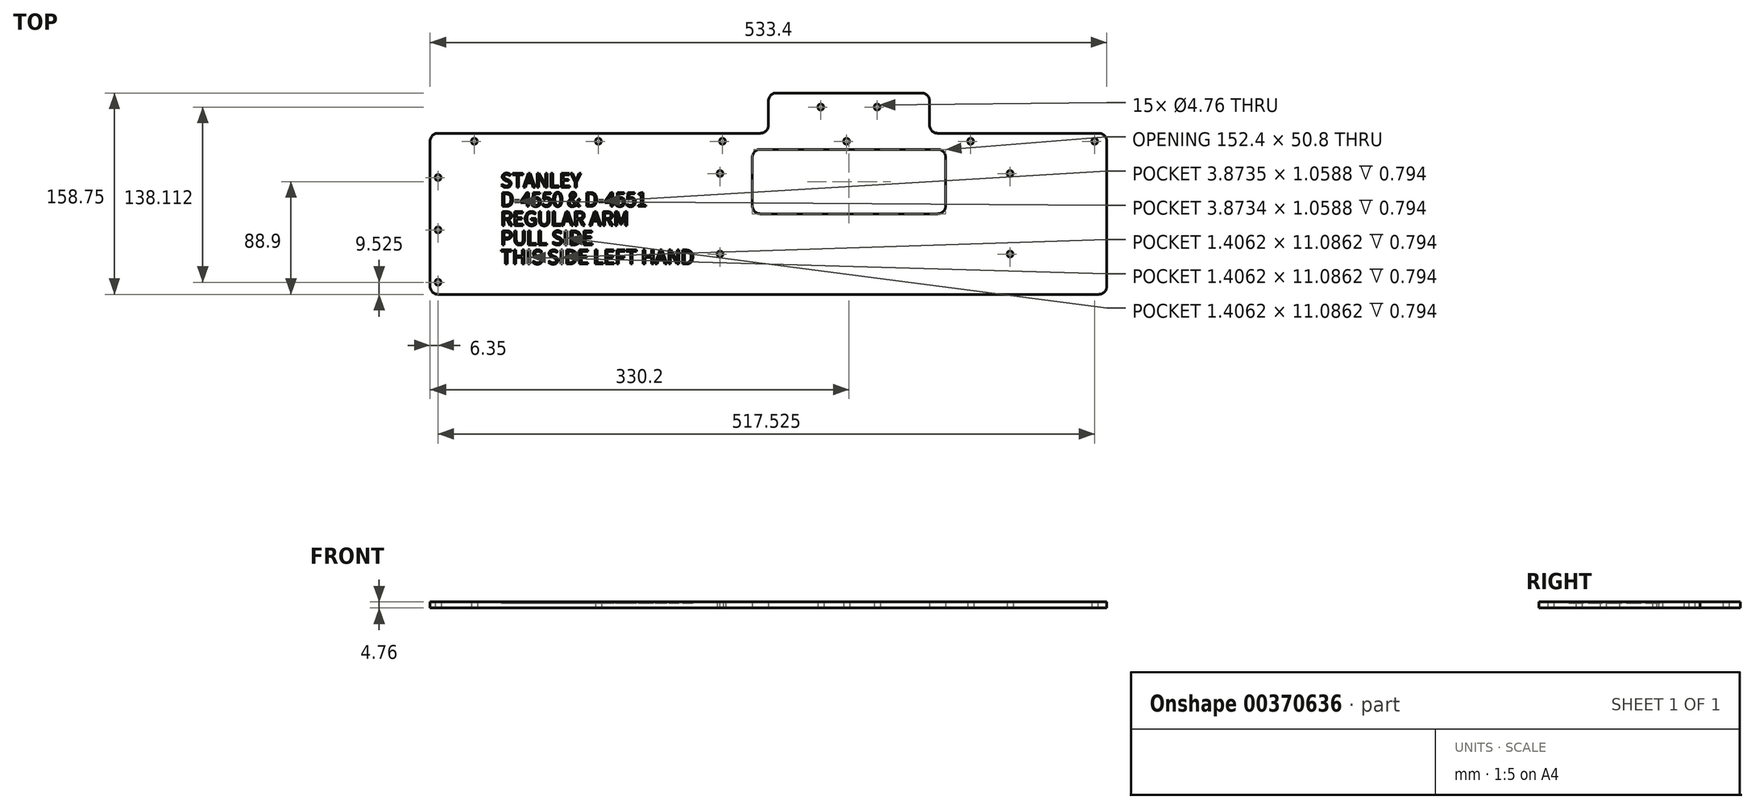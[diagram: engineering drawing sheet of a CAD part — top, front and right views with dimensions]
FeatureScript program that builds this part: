
annotation { "Feature Type Name" : "Feature", "Feature Type Description" : "" }
export const myFeature = defineFeature(function(context is Context, id is Id, definition is map)
    precondition{}
    {
        {
            var Q0;
            Q0=qCreatedBy(makeId("Top.planeOp"),FACE);
            var sketch = newSketch(context, id + "F0", { "sketchPlane" : qUnion([Q0])});
            skLineSegment(sketch, "E0.bottom", {"start": v(6.35, 0) * mm, "end": v(527.05, 0) * mm});
            skLineSegment(sketch, "E0.top", {"start": v(6.35, 127) * mm, "end": v(260.35, 127) * mm});
            skLineSegment(sketch, "E0.left", {"start": v(0, 6.35) * mm, "end": v(0, 120.65) * mm});
            skLineSegment(sketch, "E0.right", {"start": v(533.4, 6.35) * mm, "end": v(533.4, 120.65) * mm});
            skCircle(sketch, "E1", {"center": v(228.6, 95.25) * mm, "radius": 2.38 * mm});
            skCircle(sketch, "E2", {"center": v(228.6, 31.75) * mm, "radius": 2.38 * mm});
            skCircle(sketch, "E3", {"center": v(457.2, 95.25) * mm, "radius": 2.38 * mm});
            skCircle(sketch, "E4", {"center": v(457.2, 31.75) * mm, "radius": 2.38 * mm});
            skLineSegment(sketch, "E5", {"start": v(0, 114.3) * mm, "end": v(533.4, 114.3) * mm, "construction": true});
            skLineSegment(sketch, "E6.0", {"start": v(0, 101.6) * mm, "end": v(648.77, 101.6) * mm, "construction": true});
            skLineSegment(sketch, "E7.0", {"start": v(12.7, 0) * mm, "end": v(12.7, 127) * mm, "construction": true});
            skLineSegment(sketch, "E8.0", {"start": v(25.4, 0) * mm, "end": v(25.4, 127) * mm, "construction": true});
            skLineSegment(sketch, "E9.0", {"start": v(330.2, 127) * mm, "end": v(330.2, 267.26) * mm, "construction": true});
            skLineSegment(sketch, "E10.0", {"start": v(393.7, 133.35) * mm, "end": v(393.7, 152.4) * mm});
            skLineSegment(sketch, "E11.0", {"start": v(266.7, 133.35) * mm, "end": v(266.7, 152.4) * mm});
            skLineSegment(sketch, "E12.0", {"start": v(273.05, 158.75) * mm, "end": v(387.35, 158.75) * mm});
            skArc(sketch, "E13.filletArc", {"start": v(273.05, 158.75) * mm, "mid": v(268.56, 156.9) * mm, "end": v(266.7, 152.4) * mm});
            skLineSegment(sketch, "E14.trimOffspring", {"start": v(400.05, 127) * mm, "end": v(527.05, 127) * mm});
            skPoint(sketch, "E15.visualSharp", {"position": v(266.7, 127) * mm});
            skArc(sketch, "E15.filletArc", {"start": v(260.35, 127) * mm, "mid": v(264.84, 128.86) * mm, "end": v(266.7, 133.35) * mm});
            skArc(sketch, "E16.filletArc", {"start": v(393.7, 152.4) * mm, "mid": v(391.84, 156.9) * mm, "end": v(387.35, 158.75) * mm});
            skPoint(sketch, "E17.visualSharp", {"position": v(393.7, 127) * mm});
            skArc(sketch, "E17.filletArc", {"start": v(393.7, 133.35) * mm, "mid": v(395.56, 128.86) * mm, "end": v(400.05, 127) * mm});
            skCircle(sketch, "E18", {"center": v(307.98, 147.64) * mm, "radius": 2.38 * mm});
            skCircle(sketch, "E19", {"center": v(352.42, 147.64) * mm, "radius": 2.38 * mm});
            skLineSegment(sketch, "E20", {"start": v(307.98, 147.64) * mm, "end": v(352.42, 147.64) * mm, "construction": true});
            skPoint(sketch, "E21", {"position": v(330.2, 147.64) * mm});
            skPoint(sketch, "E22.visualSharp", {"position": v(0, 127) * mm});
            skArc(sketch, "E22.filletArc", {"start": v(6.35, 127) * mm, "mid": v(1.86, 125.14) * mm, "end": v(0, 120.65) * mm});
            skPoint(sketch, "E23.visualSharp", {"position": v(0, 0) * mm});
            skArc(sketch, "E23.filletArc", {"start": v(0, 6.35) * mm, "mid": v(1.86, 1.86) * mm, "end": v(6.35, 0) * mm});
            skPoint(sketch, "E24.visualSharp", {"position": v(533.4, 0) * mm});
            skArc(sketch, "E24.filletArc", {"start": v(527.05, 0) * mm, "mid": v(531.54, 1.86) * mm, "end": v(533.4, 6.35) * mm});
            skPoint(sketch, "E25.visualSharp", {"position": v(533.4, 127) * mm});
            skArc(sketch, "E25.filletArc", {"start": v(533.4, 120.65) * mm, "mid": v(531.54, 125.14) * mm, "end": v(527.05, 127) * mm});
            skCircle(sketch, "E26", {"center": v(6.35, 9.53) * mm, "radius": 2.38 * mm});
            skCircle(sketch, "E27", {"center": v(6.35, 50.8) * mm, "radius": 2.38 * mm});
            skCircle(sketch, "E28", {"center": v(6.35, 92.08) * mm, "radius": 2.38 * mm});
            skCircle(sketch, "E29", {"center": v(34.92, 120.65) * mm, "radius": 2.38 * mm});
            skCircle(sketch, "E30", {"center": v(132.72, 120.65) * mm, "radius": 2.38 * mm});
            skCircle(sketch, "E31", {"center": v(230.5, 120.65) * mm, "radius": 2.38 * mm});
            skCircle(sketch, "E32", {"center": v(328.3, 120.65) * mm, "radius": 2.38 * mm});
            skCircle(sketch, "E33", {"center": v(426.09, 120.65) * mm, "radius": 2.38 * mm});
            skCircle(sketch, "E34", {"center": v(523.88, 120.65) * mm, "radius": 2.38 * mm});
            skLineSegment(sketch, "E35", {"start": v(34.92, 120.65) * mm, "end": v(132.72, 120.65) * mm, "construction": true});
            skLineSegment(sketch, "E36", {"start": v(132.72, 120.65) * mm, "end": v(230.5, 120.65) * mm, "construction": true});
            skLineSegment(sketch, "E37", {"start": v(230.5, 120.65) * mm, "end": v(328.3, 120.65) * mm, "construction": true});
            skLineSegment(sketch, "E38", {"start": v(328.3, 120.65) * mm, "end": v(426.09, 120.65) * mm, "construction": true});
            skLineSegment(sketch, "E39", {"start": v(426.09, 120.65) * mm, "end": v(523.88, 120.65) * mm, "construction": true});
            skLineSegment(sketch, "E40", {"start": v(6.35, 92.08) * mm, "end": v(6.35, 50.8) * mm, "construction": true});
            skLineSegment(sketch, "E41", {"start": v(6.35, 50.8) * mm, "end": v(6.35, 9.53) * mm, "construction": true});
            skLineSegment(sketch, "E42.bottom", {"start": v(260.35, 114.3) * mm, "end": v(400.05, 114.3) * mm});
            skLineSegment(sketch, "E42.top", {"start": v(260.35, 63.5) * mm, "end": v(400.05, 63.5) * mm});
            skLineSegment(sketch, "E42.left", {"start": v(254, 107.95) * mm, "end": v(254, 69.85) * mm});
            skLineSegment(sketch, "E42.right", {"start": v(406.4, 107.95) * mm, "end": v(406.4, 69.85) * mm});
            skPoint(sketch, "E43.visualSharp", {"position": v(254, 114.3) * mm});
            skArc(sketch, "E43.filletArc", {"start": v(260.35, 114.3) * mm, "mid": v(255.86, 112.44) * mm, "end": v(254, 107.95) * mm});
            skPoint(sketch, "E44.visualSharp", {"position": v(254, 63.5) * mm});
            skArc(sketch, "E44.filletArc", {"start": v(254, 69.85) * mm, "mid": v(255.86, 65.36) * mm, "end": v(260.35, 63.5) * mm});
            skPoint(sketch, "E45.visualSharp", {"position": v(406.4, 63.5) * mm});
            skArc(sketch, "E45.filletArc", {"start": v(400.05, 63.5) * mm, "mid": v(404.54, 65.36) * mm, "end": v(406.4, 69.85) * mm});
            skPoint(sketch, "E46.visualSharp", {"position": v(406.4, 114.3) * mm});
            skArc(sketch, "E46.filletArc", {"start": v(406.4, 107.95) * mm, "mid": v(404.54, 112.44) * mm, "end": v(400.05, 114.3) * mm});
            skSolve(sketch);
        }
        {
            var Q0;
            Q0=qSketchRegion(id+"F0",true);
            extrude(context, id + "F1", {"entities" : qUnion([Q0]), "depth" : 4.76 * mm});
        }
        {
            var Q0;
            Q0=makeQuery(id+"F1.opExtrude","CAP_FACE",FACE,{"disambiguationData":[OSD([sQuery(id+"F0.wireOp",EDGE,"E0.bottom"),sQuery(id+"F0.wireOp",EDGE,"E0.top"),sQuery(id+"F0.wireOp",EDGE,"E0.left"),sQuery(id+"F0.wireOp",EDGE,"E0.right"),sQuery(id+"F0.wireOp",EDGE,"E1"),sQuery(id+"F0.wireOp",EDGE,"E2"),sQuery(id+"F0.wireOp",EDGE,"E3"),sQuery(id+"F0.wireOp",EDGE,"E4"),sQuery(id+"F0.wireOp",EDGE,"E10.0"),sQuery(id+"F0.wireOp",EDGE,"E11.0"),sQuery(id+"F0.wireOp",EDGE,"E12.0"),sQuery(id+"F0.wireOp",EDGE,"E13.filletArc"),sQuery(id+"F0.wireOp",EDGE,"E14.trimOffspring"),sQuery(id+"F0.wireOp",EDGE,"E15.filletArc"),sQuery(id+"F0.wireOp",EDGE,"E16.filletArc"),sQuery(id+"F0.wireOp",EDGE,"E17.filletArc"),sQuery(id+"F0.wireOp",EDGE,"E18"),sQuery(id+"F0.wireOp",EDGE,"8vzgHWK5-CGjt-0HD0-FSng-8EKi4hqDK3IT"),sQuery(id+"F0.wireOp",EDGE,"UmFmnjl2-O3XH-EXjj-iWft-K4RkXt2c9gUR"),sQuery(id+"F0.wireOp",EDGE,"E19"),sQuery(id+"F0.wireOp",EDGE,"E22.filletArc"),sQuery(id+"F0.wireOp",EDGE,"E23.filletArc"),sQuery(id+"F0.wireOp",EDGE,"E24.filletArc"),sQuery(id+"F0.wireOp",EDGE,"E25.filletArc"),sQuery(id+"F0.wireOp",EDGE,"E26"),sQuery(id+"F0.wireOp",EDGE,"E27"),sQuery(id+"F0.wireOp",EDGE,"E28"),sQuery(id+"F0.wireOp",EDGE,"E29"),sQuery(id+"F0.wireOp",EDGE,"E30"),sQuery(id+"F0.wireOp",EDGE,"E31"),sQuery(id+"F0.wireOp",EDGE,"E32"),sQuery(id+"F0.wireOp",EDGE,"E33"),sQuery(id+"F0.wireOp",EDGE,"E34")])],"isStart":false});
            var sketch = newSketch(context, id + "F2", { "sketchPlane" : qUnion([Q0])});
            skText(sketch, "E47", { "text": "STANLEY\nD-4550 & D-4551\nREGULAR ARM\nPULL SIDE\nTHIS SIDE LEFT HAND", "fontName": "NotoSansCJKjp-Regular.otf"});
            const initialGuessF2  = {"E47": [0.05559, 0.08436, 1, 0, 0.01089]};
            skSetInitialGuess(sketch, initialGuessF2);
            skSolve(sketch);
        }
        {
            var Q0;
            Q0=qSketchRegion(id+"F2",true);
            extrude(context, id + "F3", {"entities" : qUnion([Q0]), "operationType" : NewBodyOperationType.REMOVE, "oppositeDirection" : true, "depth" : 0.8 * mm});
        }
    });
